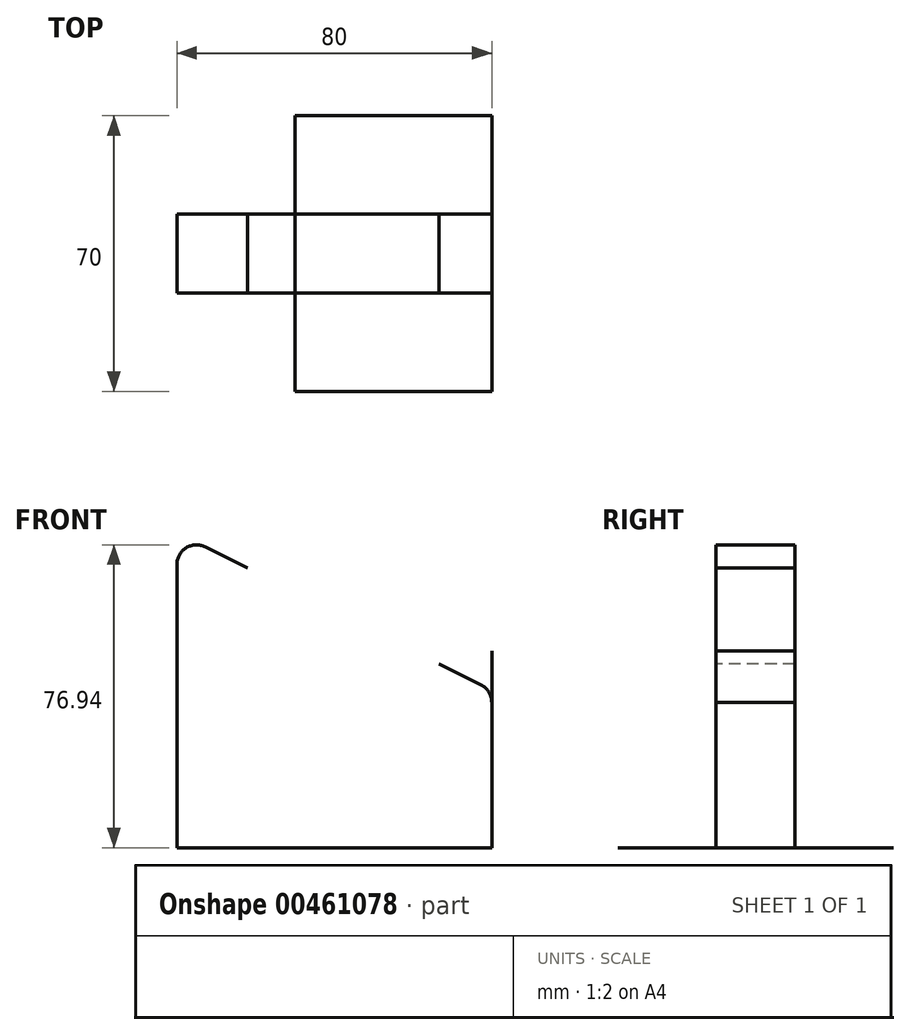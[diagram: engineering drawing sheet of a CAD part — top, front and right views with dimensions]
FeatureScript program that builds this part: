
annotation { "Feature Type Name" : "Feature", "Feature Type Description" : "" }
export const myFeature = defineFeature(function(context is Context, id is Id, definition is map)
    precondition{}
    {
        {
            var Q0;
            Q0=qCreatedBy(makeId("Front.planeOp"),FACE);
            var sketch = newSketch(context, id + "F0", { "sketchPlane" : qUnion([Q0])});
            skLineSegment(sketch, "E0", {"start": v(-44.6, 0) * mm, "end": v(35.4, 0) * mm});
            skPoint(sketch, "E1", {"position": v(35.4, 40) * mm});
            skLineSegment(sketch, "E2", {"start": v(-44.6, 0) * mm, "end": v(-44.6, 71.94) * mm});
            skLineSegment(sketch, "E3", {"start": v(32.63, 41.38) * mm, "end": v(21.98, 46.7) * mm});
            skPoint(sketch, "E4.newPointB", {"position": v(35.4, 50) * mm});
            skLineSegment(sketch, "E5", {"start": v(35.4, 36.9) * mm, "end": v(35.4, 0) * mm});
            skLineSegment(sketch, "E6", {"start": v(-37.38, 76.41) * mm, "end": v(-26.69, 71.1) * mm});
            skPoint(sketch, "E7.visualSharp", {"position": v(-44.6, 80) * mm});
            skArc(sketch, "E7.filletArc", {"start": v(-37.38, 76.41) * mm, "mid": v(-42.24, 76.19) * mm, "end": v(-44.6, 71.94) * mm});
            skArc(sketch, "E8.filletArc", {"start": v(35.4, 36.9) * mm, "mid": v(34.65, 39.54) * mm, "end": v(32.63, 41.38) * mm});
            skLineSegment(sketch, "E9", {"start": v(35.4, 50) * mm, "end": v(35.4, 0) * mm});
            skLineSegment(sketch, "E10", {"start": v(35.4, 0) * mm, "end": v(-14.6, 0) * mm});
            skLineSegment(sketch, "E11", {"start": v(-36.7, 71.1) * mm, "end": v(-16.7, 71.1) * mm});
            skSolve(sketch);
        }
        {
            var Q0;
            Q0=sQuery(id+"F0.wireOp",EDGE,"E10");
            extrude(context, id + "F1", {"bodyType" : ToolBodyType.SURFACE, "surfaceEntities" : qUnion([Q0]), "depth" : 35 * mm, "hasSecondDirection" : true, "secondDirectionOppositeDirection" : true, "secondDirectionDepth" : 35 * mm});
        }
        {
            var Q0;
            Q0=sQuery(id+"F0.wireOp",EDGE,"E9");
            extrude(context, id + "F2", {"bodyType" : ToolBodyType.SURFACE, "surfaceEntities" : qUnion([Q0]), "depth" : 10 * mm, "hasSecondDirection" : true, "secondDirectionOppositeDirection" : true, "secondDirectionDepth" : 10 * mm});
        }
        {
            var Q0;
            Q0=sQuery(id+"F0.wireOp",EDGE,"E0");
            extrude(context, id + "F3", {"bodyType" : ToolBodyType.SURFACE, "surfaceEntities" : qUnion([Q0]), "depth" : 10 * mm, "hasSecondDirection" : true, "secondDirectionOppositeDirection" : true, "secondDirectionDepth" : 10 * mm});
        }
        {
            var Q0;
            Q0=sQuery(id+"F0.wireOp",EDGE,"E2");
            var Q1;
            Q1=sQuery(id+"F0.wireOp",EDGE,"E7.filletArc");
            var Q2;
            Q2=sQuery(id+"F0.wireOp",EDGE,"E6");
            var Q3;
            Q3=sQuery(id+"F0.wireOp",EDGE,"E3");
            var Q4;
            Q4=sQuery(id+"F0.wireOp",EDGE,"E8.filletArc");
            var Q5;
            Q5=sQuery(id+"F0.wireOp",EDGE,"E0");
            extrude(context, id + "F4", {"bodyType" : ToolBodyType.SURFACE, "surfaceEntities" : qUnion([Q0, Q1, Q2, Q3, Q4, Q5]), "depth" : 10 * mm, "hasSecondDirection" : true, "secondDirectionOppositeDirection" : true, "secondDirectionDepth" : 10 * mm});
        }
    });
